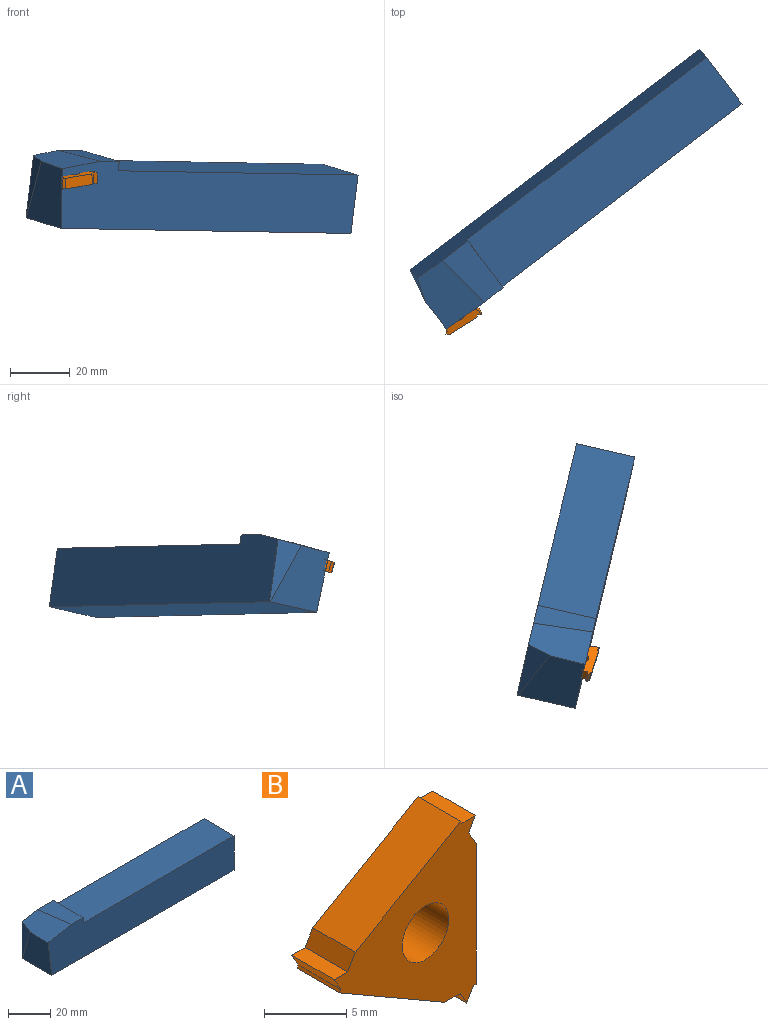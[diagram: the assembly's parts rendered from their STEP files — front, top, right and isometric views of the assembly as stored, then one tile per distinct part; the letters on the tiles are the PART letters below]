
ASSEMBLY  parts=2 mates=1
PART A: 10 faces, bbox 124.5x20x23 mm
  f0: plane 122x20mm, normal (0,0,-1), area 2440mm2, adj f1,f5,f6,f8,f9
  f1: plane 20x19.9mm, normal (1,0,0), area 398mm2, adj f0,f2,f5,f6
  f2: plane 101x20mm, normal (0,0,1), area 2020mm2, adj f1,f3,f5,f6
  f3: plane 20x3.1mm, normal (1,0,0), area 62mm2, adj f2,f4,f5,f6
  f4: plane 20x10.74mm, normal (0,0,1), area 187mm2, adj f3,f5,f6,f7
  f5: plane 124.51x23mm, normal (0,-1,0), area 2503.9mm2, adj f0,f1,f2,f3,f4,f7,f8
  f6: plane 121.9x23mm, normal (0,1,0), area 2481.5mm2, adj f0,f1,f2,f3,f4,f7,f9
  f7: plane 20x15.58mm, normal (-0.17,-0.02,0.98), area 277.4mm2, adj f4,f5,f6,f8,f9
  f8: plane 20.55x19.7mm, normal (-0.99,0,-0.12), area 326.7mm2, adj f0,f5,f7,f9
  f9: plane 21.21x7.98mm, normal (-0.95,0.31,0), area 92.3mm2, adj f0,f6,f7,f8
PART B: 18 faces, bbox 12.2x3.7x13.8 mm
  f0: plane 13.78x12.2mm, normal (0,-1,0), area 81.9mm2, adj f2,f3,f4,f5,f6,f7,f8,f9
  f1: plane 13.78x12.2mm, normal (0,1,0), area 81.9mm2, adj f2,f3,f4,f5,f6,f7,f8,f9
  f2: plane 9.04x5.22mm, normal (-0.5,0,0.87), area 38.1mm2, adj f0,f1,f13,f16
  f3: plane 9.04x5.22mm, normal (-0.5,0,-0.87), area 38.1mm2, adj f0,f1,f9,f17
  f4: plane 10.43x3.65mm, normal (1,0,0), area 38.1mm2, adj f0,f1,f6,f12
  f5: cylinder r=2mm len=4mm, axis (0,1,0), area 45.9mm2, adj f0,f1
  f6: plane 3.65x0.24mm, normal (0,0,-1), area 0.9mm2, adj f0,f1,f4,f7
  f7: plane 3.65x1mm, normal (0.87,0,-0.5), area 4.2mm2, adj f0,f1,f6,f8
  f8: plane 3.65x1mm, normal (-0.87,0,-0.5), area 4.2mm2, adj f0,f1,f7,f9
  f9: plane 3.65x1.32mm, normal (0,0,-1), area 4.8mm2, adj f0,f1,f3,f8
  f10: plane 3.65x1.15mm, normal (0,0,1), area 4.2mm2, adj f0,f1,f11,f13
  f11: plane 3.65x1mm, normal (0.87,0,-0.5), area 4.2mm2, adj f0,f1,f10,f12
  f12: plane 3.65x1.14mm, normal (0.87,0,0.5), area 4.8mm2, adj f0,f1,f4,f11
  f13: plane 3.65x0.21mm, normal (0.87,0,0.5), area 0.9mm2, adj f0,f1,f2,f10
  f14: plane 3.65x1mm, normal (-0.87,0,-0.5), area 4.2mm2, adj f0,f1,f15,f17
  f15: plane 3.65x1.15mm, normal (0,0,1), area 4.2mm2, adj f0,f1,f14,f16
  f16: plane 3.65x1.14mm, normal (-0.87,0,0.5), area 4.8mm2, adj f0,f1,f2,f15
  f17: plane 3.65x0.21mm, normal (-0.87,0,0.5), area 0.9mm2, adj f0,f1,f3,f14
PLACE A rot(axis=(0.25,0.11,0.96),38.6deg) t=(-12.74,14.39,-0.15)mm
PLACE B rot(axis=(-0.71,-0.56,0.43),95deg) t=(-45.35,-34.22,0.8)mm
MATE planar A.f7 <-> B.f5  axis (-0.01,-0.26,0.97) through (-48.73,-28.42,8.83)mm
